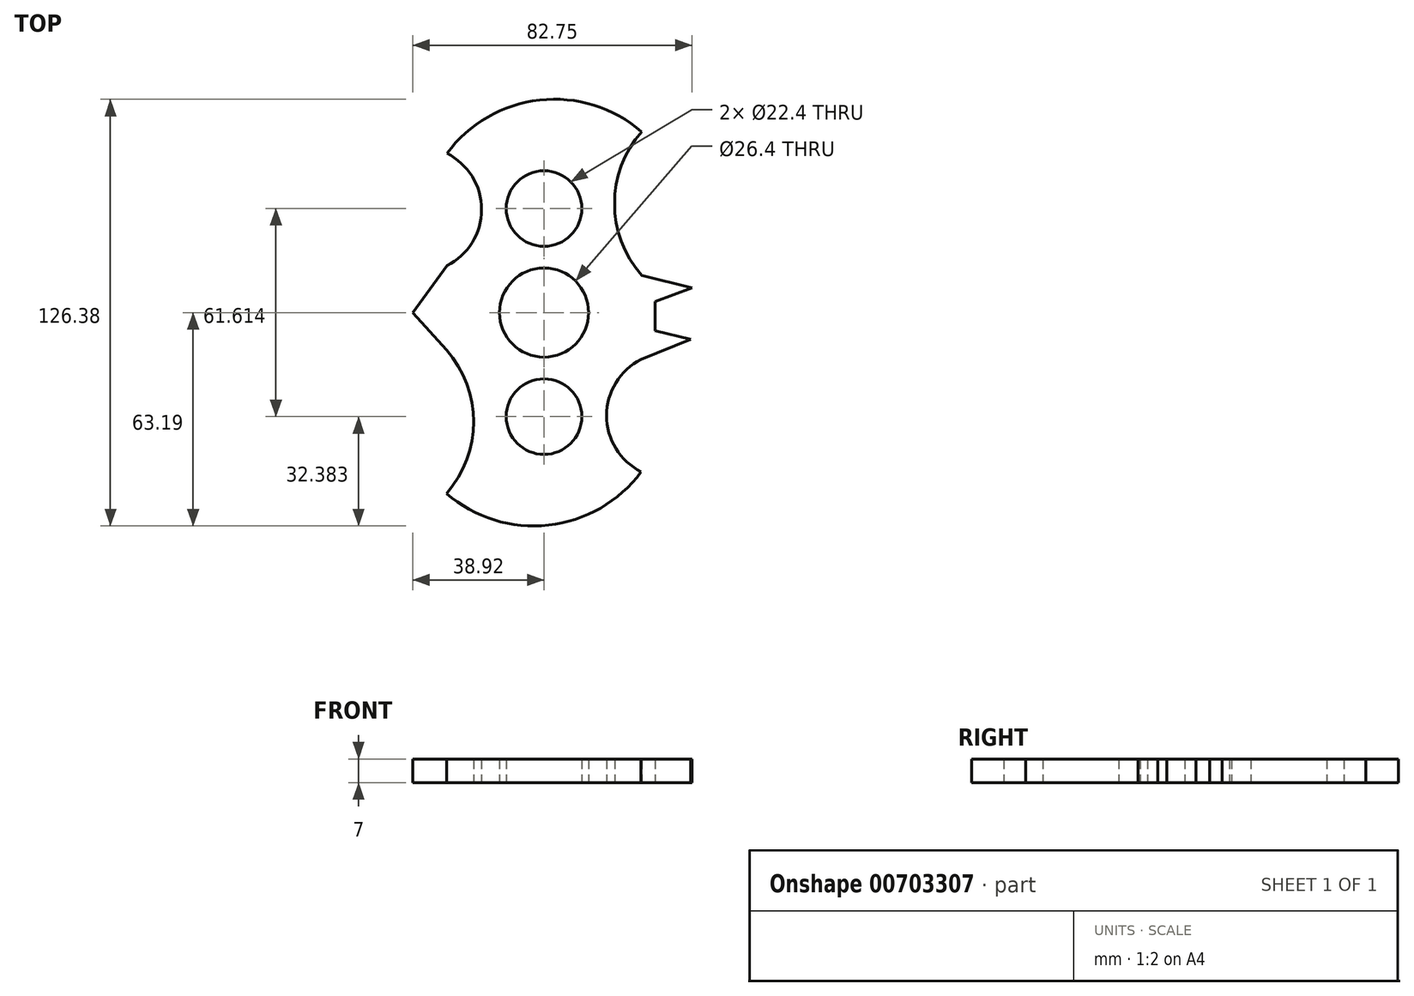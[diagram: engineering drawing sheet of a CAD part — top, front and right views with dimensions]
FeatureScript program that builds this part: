
annotation { "Feature Type Name" : "Feature", "Feature Type Description" : "" }
export const myFeature = defineFeature(function(context is Context, id is Id, definition is map)
    precondition{}
    {
        {
            var Q0;
            Q0=qCreatedBy(makeId("Top.planeOp"),FACE);
            var sketch = newSketch(context, id + "F0", { "sketchPlane" : qUnion([Q0])});
            skCircle(sketch, "E0", {"center": v(0, 0) * mm, "radius": 11.2 * mm});
            skCircle(sketch, "E1", {"center": v(0, 0) * mm, "radius": 13.2 * mm});
            skCircle(sketch, "E2", {"center": v(0, 30.8) * mm, "radius": 11.2 * mm});
            skCircle(sketch, "E3.1.0", {"center": v(0, -30.8) * mm, "radius": 11.2 * mm});
            skArc(sketch, "E4", {"start": v(28.88, 53.58) * mm, "mid": v(-1.34, 62.94) * mm, "end": v(-28.76, 47.16) * mm});
            skArc(sketch, "E5", {"start": v(-28.76, 13.87) * mm, "mid": v(-18.5, 30.51) * mm, "end": v(-28.76, 47.16) * mm});
            skArc(sketch, "E6", {"start": v(28.88, 53.58) * mm, "mid": v(20.89, 32.32) * mm, "end": v(28.88, 11.07) * mm});
            skArc(sketch, "E7.1.0", {"start": v(-28.88, -53.58) * mm, "mid": v(-20.89, -32.32) * mm, "end": v(-28.88, -11.07) * mm});
            skArc(sketch, "E7.1.1", {"start": v(-28.88, -53.58) * mm, "mid": v(1.34, -62.94) * mm, "end": v(28.76, -47.16) * mm});
            skArc(sketch, "E7.1.2", {"start": v(28.76, -13.87) * mm, "mid": v(18.5, -30.51) * mm, "end": v(28.76, -47.16) * mm});
            skPoint(sketch, "E8.start.orphan", {"position": v(-41.82, 0) * mm});
            skLineSegment(sketch, "E9", {"start": v(-28.76, 13.87) * mm, "end": v(-38.92, 0) * mm});
            skLineSegment(sketch, "E10", {"start": v(-28.88, -11.07) * mm, "end": v(-38.92, 0) * mm});
            skLineSegment(sketch, "E11", {"start": v(28.88, 11.07) * mm, "end": v(43.83, 7.33) * mm});
            skLineSegment(sketch, "E12", {"start": v(43.83, 7.33) * mm, "end": v(32.9, 3.3) * mm});
            skLineSegment(sketch, "E13", {"start": v(32.9, 3.3) * mm, "end": v(32.9, -5.32) * mm});
            skLineSegment(sketch, "E14", {"start": v(32.9, -5.32) * mm, "end": v(43.42, -7.94) * mm});
            skLineSegment(sketch, "E15", {"start": v(43.42, -7.94) * mm, "end": v(28.76, -13.87) * mm});
            skSolve(sketch);
        }
        {
            var Q0;
            Q0=makeQuery(id+"F0.imprint","IMPRINT",FACE,{"disambiguationData":[TD([[makeQuery(id+"F0.imprint","IMPRINT",EDGE,{"derivedFrom":sQuery(id+"F0.wireOp",EDGE,"E1")}),-1.0]])]});
            extrude(context, id + "F1", {"entities" : qUnion([Q0]), "depth" : 7 * mm, "offsetDistance" : 25 * mm});
        }
    });
